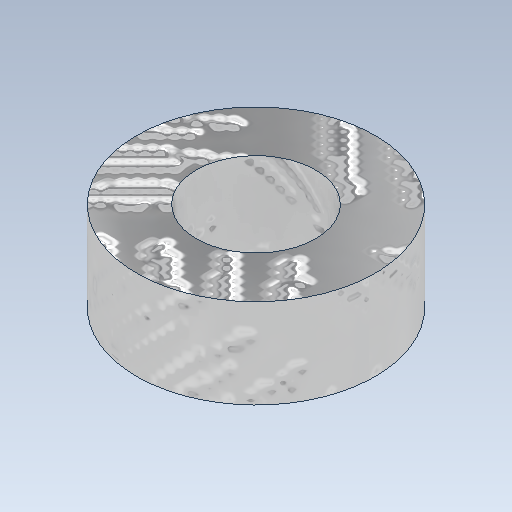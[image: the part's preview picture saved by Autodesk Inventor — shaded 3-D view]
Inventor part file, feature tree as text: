
AUTODESK INVENTOR PART (.ipt)
format: ipt  version: 2020.3 (Build 243373000, 373)  size: 164,352 bytes
history: native  units: mm
features: other x1, extrude x1, sketch x1
ambient origin geometry x8: Origin, YZ Plane, XZ Plane, XY Plane, X Axis, Y Axis, Z Axis, Center Point
bodies: Body1 (feature_tree)
feature tree (3):
  other  "ソリッド1"
  extrude  "押し出し1"  Depth=8.0mm
  sketch  "スケッチ1"
